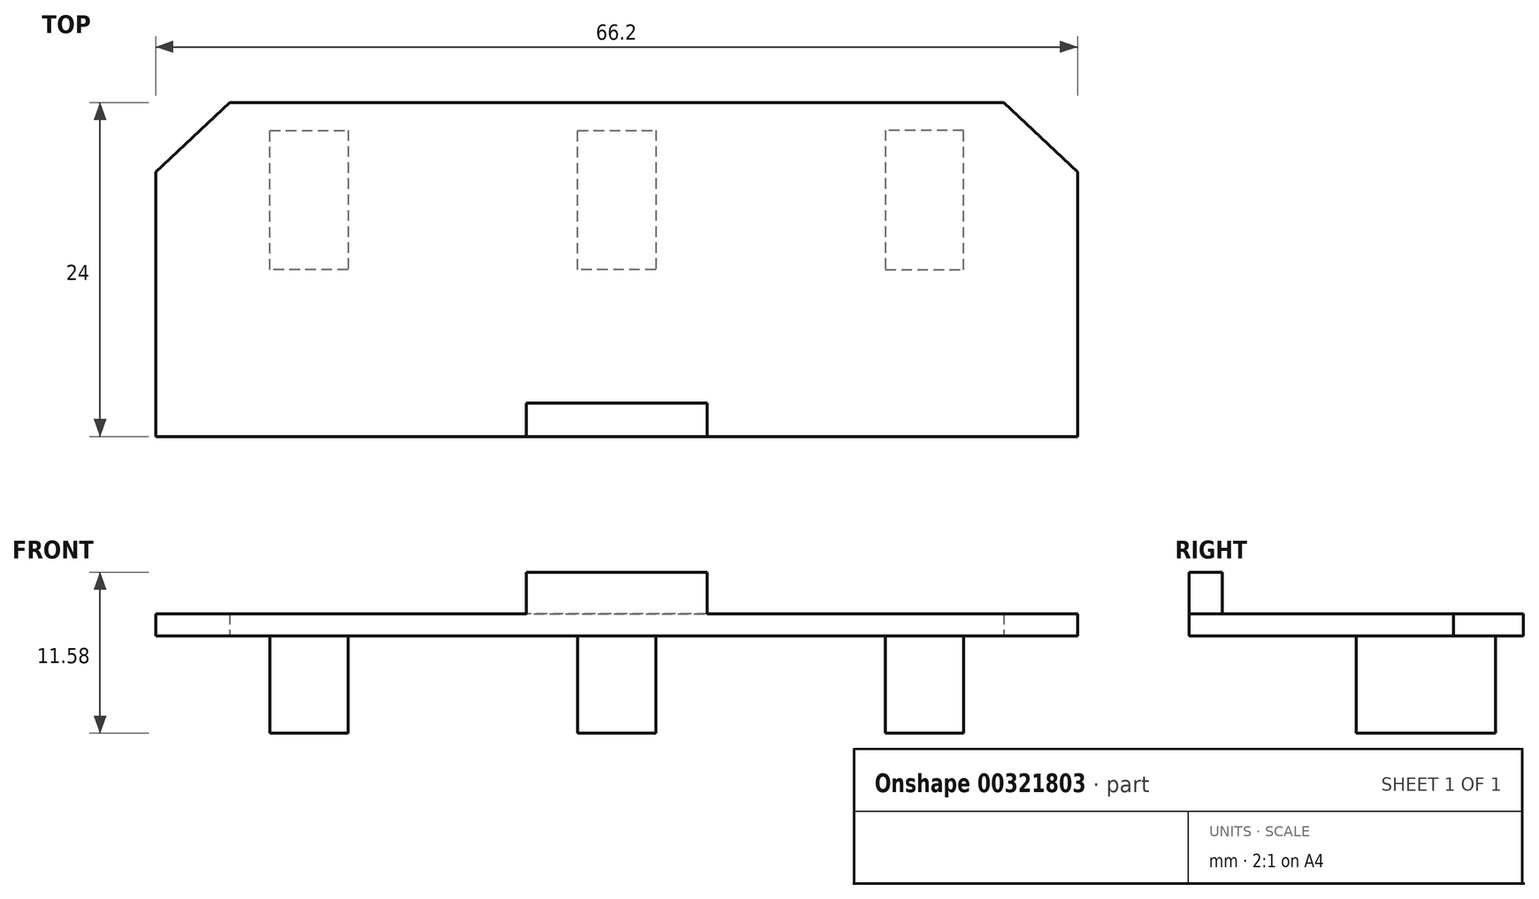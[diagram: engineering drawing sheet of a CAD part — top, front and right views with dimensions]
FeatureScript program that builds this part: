
annotation { "Feature Type Name" : "Feature", "Feature Type Description" : "" }
export const myFeature = defineFeature(function(context is Context, id is Id, definition is map)
    precondition{}
    {
        {
            var Q0;
            Q0=qCreatedBy(makeId("Top.planeOp"),FACE);
            var sketch = newSketch(context, id + "F0", { "sketchPlane" : qUnion([Q0])});
            skLineSegment(sketch, "E0.bottom", {"start": v(-22.43, 5.94) * mm, "end": v(33.17, 5.94) * mm});
            skLineSegment(sketch, "E0.top", {"start": v(-27.73, -18.06) * mm, "end": v(38.47, -18.06) * mm});
            skLineSegment(sketch, "E0.left", {"start": v(-27.73, 0.94) * mm, "end": v(-27.73, -18.06) * mm});
            skLineSegment(sketch, "E0.right", {"start": v(38.47, 0.94) * mm, "end": v(38.47, -18.06) * mm});
            skLineSegment(sketch, "E1", {"start": v(38.47, 0.94) * mm, "end": v(33.17, 5.94) * mm});
            skLineSegment(sketch, "E2.MirrorCS", {"start": v(-27.73, 0.94) * mm, "end": v(-22.43, 5.94) * mm});
            skLineSegment(sketch, "E3", {"start": v(5.37, 3.94) * mm, "end": v(8.17, 3.94) * mm});
            skLineSegment(sketch, "E4", {"start": v(8.17, 3.94) * mm, "end": v(8.17, -6.06) * mm});
            skLineSegment(sketch, "E5", {"start": v(8.17, -6.06) * mm, "end": v(2.57, -6.06) * mm});
            skLineSegment(sketch, "E6", {"start": v(2.57, -6.06) * mm, "end": v(2.57, 3.94) * mm});
            skLineSegment(sketch, "E7", {"start": v(2.57, 3.94) * mm, "end": v(8.17, 3.94) * mm});
            skLineSegment(sketch, "E8", {"start": v(24.67, 3.94) * mm, "end": v(24.67, -6.06) * mm});
            skLineSegment(sketch, "E9", {"start": v(24.67, -6.06) * mm, "end": v(30.27, -6.06) * mm});
            skLineSegment(sketch, "E10", {"start": v(30.27, -6.06) * mm, "end": v(30.27, 3.94) * mm});
            skLineSegment(sketch, "E11", {"start": v(30.27, 3.94) * mm, "end": v(24.67, 3.94) * mm});
            skLineSegment(sketch, "E12.MirrorCS", {"start": v(-13.93, 3.94) * mm, "end": v(-13.93, -6.06) * mm});
            skLineSegment(sketch, "E13.MirrorCS", {"start": v(-19.53, 3.94) * mm, "end": v(-13.93, 3.94) * mm});
            skLineSegment(sketch, "E14.MirrorCS", {"start": v(-19.53, -6.06) * mm, "end": v(-19.53, 3.94) * mm});
            skLineSegment(sketch, "E15.MirrorCS", {"start": v(-13.93, -6.06) * mm, "end": v(-19.53, -6.06) * mm});
            skSolve(sketch);
        }
        {
            var Q0;
            Q0=makeQuery(id+"F0.imprint","IMPRINT",FACE,{"disambiguationData":[TD([[makeQuery(id+"F0.imprint","IMPRINT",EDGE,{"derivedFrom":sQuery(id+"F0.wireOp",EDGE,"E12.MirrorCS")}),-1.0]])]});
            var Q1;
            {var subQ3=sQuery(id+"F0.wireOp",EDGE,"E4");Q1=makeQuery(id+"F0.imprint","IMPRINT",FACE,{"disambiguationData":[TD([[makeQuery(id+"F0.imprint","IMPRINT",EDGE,{"derivedFrom":subQ3}),-1.0]])]});}
            var Q2;
            Q2=makeQuery(id+"F0.imprint","IMPRINT",FACE,{"disambiguationData":[TD([[makeQuery(id+"F0.imprint","IMPRINT",EDGE,{"derivedFrom":sQuery(id+"F0.wireOp",EDGE,"E8")}),1.0]])]});
            extrude(context, id + "F1", {"entities" : qUnion([Q0, Q1, Q2]), "oppositeDirection" : true, "depth" : 7 * mm});
        }
        {
            var Q0;
            Q0 = qSketchRegion(id + "F0", true);
            var Q1;
            Q1=makeQuery(id+"F0.imprint","IMPRINT",FACE,{"disambiguationData":[TD([[makeQuery(id+"F0.imprint","IMPRINT",EDGE,{"derivedFrom":sQuery(id+"F0.wireOp",EDGE,"E0.bottom")}),-1.0]])]});
            var Q2;
            Q2=makeQuery(id+"F0.imprint","IMPRINT",FACE,{"disambiguationData":[TD([[makeQuery(id+"F0.imprint","IMPRINT",EDGE,{"derivedFrom":sQuery(id+"F0.wireOp",EDGE,"E12.MirrorCS")}),-1.0]])]});
            var Q3;
            {var subQ3=sQuery(id+"F0.wireOp",EDGE,"E4");Q3=makeQuery(id+"F0.imprint","IMPRINT",FACE,{"disambiguationData":[TD([[makeQuery(id+"F0.imprint","IMPRINT",EDGE,{"derivedFrom":subQ3}),-1.0]])]});}
            var Q4;
            Q4=makeQuery(id+"F0.imprint","IMPRINT",FACE,{"disambiguationData":[TD([[makeQuery(id+"F0.imprint","IMPRINT",EDGE,{"derivedFrom":sQuery(id+"F0.wireOp",EDGE,"E8")}),1.0]])]});
            extrude(context, id + "F2", {"entities" : qUnion([Q0, Q1, Q2, Q3, Q4]), "operationType" : NewBodyOperationType.ADD, "depth" : 1.58 * mm});
        }
        {
            var Q0;
            Q0=makeQuery(id+"F2.opExtrude","CAP_FACE",FACE,{"disambiguationData":[OSD([sQuery(id+"F0.wireOp",EDGE,"E0.bottom"),sQuery(id+"F0.wireOp",EDGE,"E0.top"),sQuery(id+"F0.wireOp",EDGE,"E0.left"),sQuery(id+"F0.wireOp",EDGE,"E0.right"),sQuery(id+"F0.wireOp",EDGE,"E1"),sQuery(id+"F0.wireOp",EDGE,"E2.MirrorCS")])],"isStart":false});
            var sketch = newSketch(context, id + "F3", { "sketchPlane" : qUnion([Q0])});
            skLineSegment(sketch, "E16", {"start": v(5.37, -18.06) * mm, "end": v(11.87, -18.06) * mm});
            skLineSegment(sketch, "E17", {"start": v(11.87, -18.06) * mm, "end": v(11.87, -15.66) * mm});
            skLineSegment(sketch, "E18", {"start": v(11.87, -15.66) * mm, "end": v(-1.13, -15.66) * mm});
            skLineSegment(sketch, "E19", {"start": v(-1.13, -15.66) * mm, "end": v(-1.13, -18.06) * mm});
            skLineSegment(sketch, "E20", {"start": v(-1.13, -18.06) * mm, "end": v(11.87, -18.06) * mm});
            skSolve(sketch);
        }
        {
            var Q0;
            {var subQ0=sQuery(id+"F3.wireOp",EDGE,"E17");Q0=makeQuery(id+"F3.imprint","IMPRINT",FACE,{"disambiguationData":[TD([[makeQuery(id+"F3.imprint","IMPRINT",EDGE,{"derivedFrom":subQ0}),1.0]])]});}
            extrude(context, id + "F4", {"entities" : qUnion([Q0]), "operationType" : NewBodyOperationType.ADD, "depth" : 3 * mm});
        }
    });
